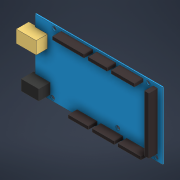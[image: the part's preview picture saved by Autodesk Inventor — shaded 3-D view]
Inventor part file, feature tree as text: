
AUTODESK INVENTOR PART (.ipt)
format: ipt  version: 2021 (Build 250183000, 183)  size: 228,864 bytes
history: native  units: mm
features: extrude x5, sketch x1
ambient origin geometry x8: Origin, YZ Plane, XZ Plane, XY Plane, X Axis, Y Axis, Z Axis, Center Point
bodies: Volumenkörper1 (feature_tree)
feature tree (6):
  sketch  "Skizze1"  dims[d0=101.6mm d1=53.34mm d2=3.2mm d3=15.24mm d4=3.2mm d5=13.97mm d6=2.54mm d7=48.26mm d8=3.2mm d9=90.17mm d10=3.2mm d11=96.52mm d12=3.2mm d13=66.04mm d14=7.62mm d15=25.0mm d16=4.0mm d17=15.0mm d18=2.5mm d19=18.5mm d20=3.5mm d21=45.0mm d22=4.0mm d23=2.5mm d24=4.0mm d25=9.0mm d26=10.0mm d27=16.0mm d28=6.0mm d29=8.5mm d30=3.5mm d31=14.0mm d32=2.0mm d33=1.0mm d34=0.0mm d35=8.0mm d36=0.0mm d37=8.0mm d38=0.0mm d41=10.0mm d42=0.0mm d43=10.0mm d44=0.0mm d39=0.5mm d40=0.872665mm]
  extrude  "Extrusion1"  Depth=53.34mm
  extrude  "Extrusion2"  Depth=0.5mm
  extrude  "Extrusion3"  Depth=0.5mm
  extrude  "Extrusion5"  Depth=0.5mm
  extrude  "Extrusion6"  Depth=0.5mm
